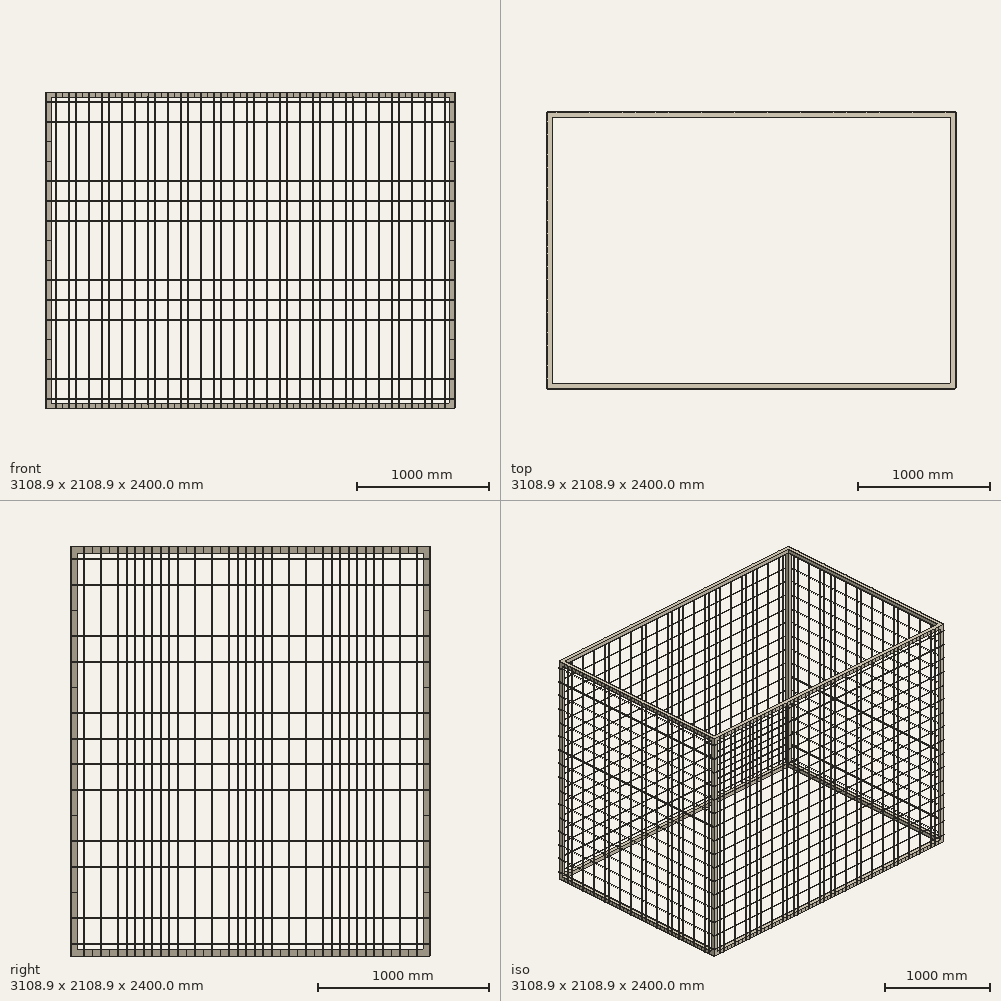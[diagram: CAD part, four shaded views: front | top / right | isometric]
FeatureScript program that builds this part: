
annotation { "Feature Type Name" : "Feature", "Feature Type Description" : "" }
export const myFeature = defineFeature(function(context is Context, id is Id, definition is map)
    precondition{}
    {
        {
            var Q0;
            Q0=qCreatedBy(makeId("Top.planeOp"),FACE);
            var sketch = newSketch(context, id + "F0", { "sketchPlane" : qUnion([Q0])});
            skLineSegment(sketch, "E0", {"start": v(-1510, 0) * mm, "end": v(-1550, 0) * mm});
            skLineSegment(sketch, "E1", {"start": v(-1550, 0) * mm, "end": v(-1550, -1050) * mm});
            skLineSegment(sketch, "E2", {"start": v(-1550, -1050) * mm, "end": v(0, -1050) * mm});
            skLineSegment(sketch, "E3", {"start": v(0, -1050) * mm, "end": v(0, -1010) * mm});
            skLineSegment(sketch, "E4", {"start": v(0, -1010) * mm, "end": v(-1510, -1010) * mm});
            skLineSegment(sketch, "E5", {"start": v(-1510, 0) * mm, "end": v(-1510, -1010) * mm});
            skLineSegment(sketch, "E6", {"start": v(0, 0) * mm, "end": v(0, 100.18) * mm, "construction": true});
            skLineSegment(sketch, "E7", {"start": v(0, 0) * mm, "end": v(-123.05, 0) * mm, "construction": true});
            skSolve(sketch);
        }
        {
            var Q0;
            Q0 = qSketchRegion(id + "F0", true);
            extrude(context, id + "F1", {"entities" : qUnion([Q0]), "depth" : 40 * mm});
        }
        {
            var Q0;
            Q0=qCreatedBy(makeId("Top.planeOp"),FACE);
            var sketch = newSketch(context, id + "F2", { "sketchPlane" : qUnion([Q0])});
            skLineSegment(sketch, "E8.bottom", {"start": v(-1550, -1010) * mm, "end": v(-1510, -1010) * mm});
            skLineSegment(sketch, "E8.top", {"start": v(-1550, -1050) * mm, "end": v(-1510, -1050) * mm});
            skLineSegment(sketch, "E8.left", {"start": v(-1550, -1010) * mm, "end": v(-1550, -1050) * mm});
            skLineSegment(sketch, "E8.right", {"start": v(-1510, -1010) * mm, "end": v(-1510, -1050) * mm});
            skSolve(sketch);
        }
        {
            var Q0;
            Q0 = qSketchRegion(id + "F2", true);
            extrude(context, id + "F3", {"entities" : qUnion([Q0]), "operationType" : NewBodyOperationType.ADD, "depth" : 1200 * mm});
        }
        {
            var Q0;
            Q0=qCreatedBy(makeId("Top.planeOp"),FACE);
            var sketch = newSketch(context, id + "F4", { "sketchPlane" : qUnion([Q0])});
            skCircle(sketch, "E9", {"center": v(-1552.2, -25) * mm, "radius": 2.25 * mm});
            skLineSegment(sketch, "E10", {"start": v(-121.65, 0) * mm, "end": v(-1550, 0) * mm, "construction": true});
            skLineSegment(sketch, "E11", {"start": v(0, -80.6) * mm, "end": v(0, -1050) * mm, "construction": true});
            skCircle(sketch, "E12", {"center": v(-25, -1052.2) * mm, "radius": 2.25 * mm});
            skCircle(sketch, "E13.1.0.0", {"center": v(-75, -1052.2) * mm, "radius": 2.25 * mm});
            skCircle(sketch, "E13.2.0.0", {"center": v(-125, -1052.2) * mm, "radius": 2.25 * mm});
            skCircle(sketch, "E13.3.0.0", {"center": v(-175, -1052.2) * mm, "radius": 2.25 * mm});
            skCircle(sketch, "E13.4.0.0", {"center": v(-225, -1052.2) * mm, "radius": 2.25 * mm});
            skCircle(sketch, "E13.5.0.0", {"center": v(-275, -1052.2) * mm, "radius": 2.25 * mm});
            skCircle(sketch, "E13.6.0.0", {"center": v(-325, -1052.2) * mm, "radius": 2.25 * mm});
            skCircle(sketch, "E13.7.0.0", {"center": v(-375, -1052.2) * mm, "radius": 2.25 * mm});
            skCircle(sketch, "E13.8.0.0", {"center": v(-425, -1052.2) * mm, "radius": 2.25 * mm});
            skCircle(sketch, "E13.9.0.0", {"center": v(-475, -1052.2) * mm, "radius": 2.25 * mm});
            skCircle(sketch, "E13.10.0.0", {"center": v(-525, -1052.2) * mm, "radius": 2.25 * mm});
            skCircle(sketch, "E13.11.0.0", {"center": v(-575, -1052.2) * mm, "radius": 2.25 * mm});
            skCircle(sketch, "E13.12.0.0", {"center": v(-625, -1052.2) * mm, "radius": 2.25 * mm});
            skCircle(sketch, "E13.13.0.0", {"center": v(-675, -1052.2) * mm, "radius": 2.25 * mm});
            skCircle(sketch, "E13.14.0.0", {"center": v(-725, -1052.2) * mm, "radius": 2.25 * mm});
            skCircle(sketch, "E13.15.0.0", {"center": v(-775, -1052.2) * mm, "radius": 2.25 * mm});
            skCircle(sketch, "E13.16.0.0", {"center": v(-825, -1052.2) * mm, "radius": 2.25 * mm});
            skCircle(sketch, "E13.17.0.0", {"center": v(-875, -1052.2) * mm, "radius": 2.25 * mm});
            skCircle(sketch, "E13.18.0.0", {"center": v(-925, -1052.2) * mm, "radius": 2.25 * mm});
            skCircle(sketch, "E13.19.0.0", {"center": v(-975, -1052.2) * mm, "radius": 2.25 * mm});
            skCircle(sketch, "E13.20.0.0", {"center": v(-1025, -1052.2) * mm, "radius": 2.25 * mm});
            skCircle(sketch, "E13.21.0.0", {"center": v(-1075, -1052.2) * mm, "radius": 2.25 * mm});
            skCircle(sketch, "E13.22.0.0", {"center": v(-1125, -1052.2) * mm, "radius": 2.25 * mm});
            skCircle(sketch, "E13.23.0.0", {"center": v(-1175, -1052.2) * mm, "radius": 2.25 * mm});
            skCircle(sketch, "E13.24.0.0", {"center": v(-1225, -1052.2) * mm, "radius": 2.25 * mm});
            skCircle(sketch, "E13.25.0.0", {"center": v(-1275, -1052.2) * mm, "radius": 2.25 * mm});
            skCircle(sketch, "E13.26.0.0", {"center": v(-1325, -1052.2) * mm, "radius": 2.25 * mm});
            skCircle(sketch, "E13.27.0.0", {"center": v(-1375, -1052.2) * mm, "radius": 2.25 * mm});
            skCircle(sketch, "E13.28.0.0", {"center": v(-1425, -1052.2) * mm, "radius": 2.25 * mm});
            skCircle(sketch, "E13.29.0.0", {"center": v(-1475, -1052.2) * mm, "radius": 2.25 * mm});
            skLineSegment(sketch, "E13.direction1", {"start": v(-25, -1052.2) * mm, "end": v(-75, -1052.2) * mm, "construction": true});
            skCircle(sketch, "E14.0.1.0", {"center": v(-1552.2, -75) * mm, "radius": 2.25 * mm});
            skCircle(sketch, "E14.0.2.0", {"center": v(-1552.2, -125) * mm, "radius": 2.25 * mm});
            skCircle(sketch, "E14.0.3.0", {"center": v(-1552.2, -175) * mm, "radius": 2.25 * mm});
            skCircle(sketch, "E14.0.4.0", {"center": v(-1552.2, -225) * mm, "radius": 2.25 * mm});
            skCircle(sketch, "E14.0.5.0", {"center": v(-1552.2, -275) * mm, "radius": 2.25 * mm});
            skCircle(sketch, "E14.0.6.0", {"center": v(-1552.2, -325) * mm, "radius": 2.25 * mm});
            skCircle(sketch, "E14.0.7.0", {"center": v(-1552.2, -375) * mm, "radius": 2.25 * mm});
            skCircle(sketch, "E14.0.8.0", {"center": v(-1552.2, -425) * mm, "radius": 2.25 * mm});
            skCircle(sketch, "E14.0.9.0", {"center": v(-1552.2, -475) * mm, "radius": 2.25 * mm});
            skCircle(sketch, "E14.0.10.0", {"center": v(-1552.2, -525) * mm, "radius": 2.25 * mm});
            skCircle(sketch, "E14.0.11.0", {"center": v(-1552.2, -575) * mm, "radius": 2.25 * mm});
            skCircle(sketch, "E14.0.12.0", {"center": v(-1552.2, -625) * mm, "radius": 2.25 * mm});
            skCircle(sketch, "E14.0.13.0", {"center": v(-1552.2, -675) * mm, "radius": 2.25 * mm});
            skCircle(sketch, "E14.0.14.0", {"center": v(-1552.2, -725) * mm, "radius": 2.25 * mm});
            skCircle(sketch, "E14.0.15.0", {"center": v(-1552.2, -775) * mm, "radius": 2.25 * mm});
            skCircle(sketch, "E14.0.16.0", {"center": v(-1552.2, -825) * mm, "radius": 2.25 * mm});
            skCircle(sketch, "E14.0.17.0", {"center": v(-1552.2, -875) * mm, "radius": 2.25 * mm});
            skCircle(sketch, "E14.0.18.0", {"center": v(-1552.2, -925) * mm, "radius": 2.25 * mm});
            skCircle(sketch, "E14.0.19.0", {"center": v(-1552.2, -975) * mm, "radius": 2.25 * mm});
            skLineSegment(sketch, "E14.direction1", {"start": v(-1552.2, -25) * mm, "end": v(-1527.2, -25) * mm, "construction": true});
            skLineSegment(sketch, "E14.direction2", {"start": v(-1552.2, -25) * mm, "end": v(-1552.2, -75) * mm, "construction": true});
            skSolve(sketch);
        }
        {
            var Q0;
            Q0 = qSketchRegion(id + "F4", true);
            var Q1;
            Q1=makeQuery(id+"F3.opExtrude","CAP_FACE",FACE,{"disambiguationData":[OSD([sQuery(id+"F2.wireOp",EDGE,"E8.bottom"),sQuery(id+"F2.wireOp",EDGE,"E8.top"),sQuery(id+"F2.wireOp",EDGE,"E8.left"),sQuery(id+"F2.wireOp",EDGE,"E8.right")])],"isStart":false});
            extrude(context, id + "F5", {"entities" : qUnion([Q0]), "operationType" : NewBodyOperationType.ADD, "endBound" : BoundingType.UP_TO_SURFACE, "endBoundEntityFace" : qUnion([Q1]), "depth" : 25 * mm});
        }
        {
            var Q0;
            Q0=qCreatedBy(makeId("Front.planeOp"),FACE);
            var sketch = newSketch(context, id + "F6", { "sketchPlane" : qUnion([Q0])});
            skLineSegment(sketch, "E15.0", {"start": v(-1554.45, 1200) * mm, "end": v(-1549.95, 1200) * mm, "construction": true});
            skLineSegment(sketch, "E16", {"start": v(-1554.45, 1200) * mm, "end": v(-1554.45, 1217.11) * mm, "construction": true});
            skLineSegment(sketch, "E17", {"start": v(-1549.95, 1200) * mm, "end": v(-1549.95, 1218.1) * mm, "construction": true});
            skCircle(sketch, "E18", {"center": v(-1552.2, 1125) * mm, "radius": 2.25 * mm});
            skCircle(sketch, "E19.0.1.0", {"center": v(-1552.2, 975) * mm, "radius": 2.25 * mm});
            skCircle(sketch, "E19.0.2.0", {"center": v(-1552.2, 825) * mm, "radius": 2.25 * mm});
            skCircle(sketch, "E19.0.3.0", {"center": v(-1552.2, 675) * mm, "radius": 2.25 * mm});
            skCircle(sketch, "E19.0.4.0", {"center": v(-1552.2, 525) * mm, "radius": 2.25 * mm});
            skCircle(sketch, "E19.0.5.0", {"center": v(-1552.2, 375) * mm, "radius": 2.25 * mm});
            skCircle(sketch, "E19.0.6.0", {"center": v(-1552.2, 225) * mm, "radius": 2.25 * mm});
            skCircle(sketch, "E19.0.7.0", {"center": v(-1552.2, 75) * mm, "radius": 2.25 * mm});
            skLineSegment(sketch, "E19.direction1", {"start": v(-1552.2, 1125) * mm, "end": v(-1527.2, 1125) * mm, "construction": true});
            skLineSegment(sketch, "E19.direction2", {"start": v(-1552.2, 1125) * mm, "end": v(-1552.2, 975) * mm, "construction": true});
            skSolve(sketch);
        }
        {
            var Q0;
            Q0 = qSketchRegion(id + "F6", true);
            var Q1;
            {var subQ0=sQuery(id+"F4.wireOp",EDGE,"E13.29.0.0");var subQ1=sQuery(id+"F0.wireOp",EDGE,"E1");var subQ2=sQuery(id+"F0.wireOp",EDGE,"E5");var subQ3=sQuery(id+"F0.wireOp",EDGE,"E4");var subQ4=sQuery(id+"F0.wireOp",EDGE,"E3");var subQ5=sQuery(id+"F0.wireOp",EDGE,"E2");var subQ6=sQuery(id+"F0.wireOp",EDGE,"E0");var subQ7=sQuery(id+"F2.wireOp",EDGE,"E8.left");var subQ8=sQuery(id+"F2.wireOp",EDGE,"E8.right");var subQ9=sQuery(id+"F2.wireOp",EDGE,"E8.top");Q1=makeQuery(id+"F5.boolean.opBoolean","SPLIT",FACE,{"disambiguationData":[TD([makeQuery(id+"F1.opExtrude","CAP_FACE",FACE,{"disambiguationData":[OSD([subQ6,subQ1,subQ5,subQ4,subQ3,subQ2])],"isStart":true}),makeQuery(id+"F1.opExtrude","CAP_FACE",FACE,{"disambiguationData":[OSD([subQ6,subQ1,subQ5,subQ4,subQ3,subQ2])],"isStart":false}),makeQuery(id+"F1.opExtrude","SWEPT_FACE",FACE,{"disambiguationData":[OSD([subQ1])]}),makeQuery(id+"F3.opExtrude","CAP_FACE",FACE,{"disambiguationData":[OSD([sQuery(id+"F2.wireOp",EDGE,"E8.bottom"),subQ9,subQ7,subQ8])],"isStart":false}),makeQuery(id+"F3.opExtrude","SWEPT_FACE",FACE,{"disambiguationData":[OSD([subQ7])]}),makeQuery(id+"F3.opExtrude","SWEPT_FACE",FACE,{"disambiguationData":[OSD([subQ8])]}),makeQuery(id+"F5.opExtrude","CAP_FACE",FACE,{"disambiguationData":[OSD([sQuery(id+"F4.wireOp",EDGE,"E9")])],"isStart":true}),makeQuery(id+"F5.opExtrude","CAP_FACE",FACE,{"disambiguationData":[OSD([sQuery(id+"F4.wireOp",EDGE,"E12")])],"isStart":true}),makeQuery(id+"F5.opExtrude","CAP_FACE",FACE,{"disambiguationData":[OSD([sQuery(id+"F4.wireOp",EDGE,"E13.1.0.0")])],"isStart":true}),makeQuery(id+"F5.opExtrude","CAP_FACE",FACE,{"disambiguationData":[OSD([sQuery(id+"F4.wireOp",EDGE,"E13.2.0.0")])],"isStart":true}),makeQuery(id+"F5.opExtrude","CAP_FACE",FACE,{"disambiguationData":[OSD([sQuery(id+"F4.wireOp",EDGE,"E13.3.0.0")])],"isStart":true}),makeQuery(id+"F5.opExtrude","CAP_FACE",FACE,{"disambiguationData":[OSD([sQuery(id+"F4.wireOp",EDGE,"E13.4.0.0")])],"isStart":true}),makeQuery(id+"F5.opExtrude","CAP_FACE",FACE,{"disambiguationData":[OSD([sQuery(id+"F4.wireOp",EDGE,"E13.5.0.0")])],"isStart":true}),makeQuery(id+"F5.opExtrude","CAP_FACE",FACE,{"disambiguationData":[OSD([sQuery(id+"F4.wireOp",EDGE,"E13.6.0.0")])],"isStart":true}),makeQuery(id+"F5.opExtrude","CAP_FACE",FACE,{"disambiguationData":[OSD([sQuery(id+"F4.wireOp",EDGE,"E13.7.0.0")])],"isStart":true}),makeQuery(id+"F5.opExtrude","CAP_FACE",FACE,{"disambiguationData":[OSD([sQuery(id+"F4.wireOp",EDGE,"E13.8.0.0")])],"isStart":true}),makeQuery(id+"F5.opExtrude","CAP_FACE",FACE,{"disambiguationData":[OSD([sQuery(id+"F4.wireOp",EDGE,"E13.9.0.0")])],"isStart":true}),makeQuery(id+"F5.opExtrude","CAP_FACE",FACE,{"disambiguationData":[OSD([sQuery(id+"F4.wireOp",EDGE,"E13.10.0.0")])],"isStart":true}),makeQuery(id+"F5.opExtrude","CAP_FACE",FACE,{"disambiguationData":[OSD([sQuery(id+"F4.wireOp",EDGE,"E13.11.0.0")])],"isStart":true}),makeQuery(id+"F5.opExtrude","CAP_FACE",FACE,{"disambiguationData":[OSD([sQuery(id+"F4.wireOp",EDGE,"E13.12.0.0")])],"isStart":true}),makeQuery(id+"F5.opExtrude","CAP_FACE",FACE,{"disambiguationData":[OSD([sQuery(id+"F4.wireOp",EDGE,"E13.13.0.0")])],"isStart":true}),makeQuery(id+"F5.opExtrude","CAP_FACE",FACE,{"disambiguationData":[OSD([sQuery(id+"F4.wireOp",EDGE,"E13.14.0.0")])],"isStart":true}),makeQuery(id+"F5.opExtrude","CAP_FACE",FACE,{"disambiguationData":[OSD([sQuery(id+"F4.wireOp",EDGE,"E13.15.0.0")])],"isStart":true}),makeQuery(id+"F5.opExtrude","CAP_FACE",FACE,{"disambiguationData":[OSD([sQuery(id+"F4.wireOp",EDGE,"E13.16.0.0")])],"isStart":true}),makeQuery(id+"F5.opExtrude","CAP_FACE",FACE,{"disambiguationData":[OSD([sQuery(id+"F4.wireOp",EDGE,"E13.17.0.0")])],"isStart":true}),makeQuery(id+"F5.opExtrude","CAP_FACE",FACE,{"disambiguationData":[OSD([sQuery(id+"F4.wireOp",EDGE,"E13.18.0.0")])],"isStart":true}),makeQuery(id+"F5.opExtrude","CAP_FACE",FACE,{"disambiguationData":[OSD([sQuery(id+"F4.wireOp",EDGE,"E13.19.0.0")])],"isStart":true}),makeQuery(id+"F5.opExtrude","CAP_FACE",FACE,{"disambiguationData":[OSD([sQuery(id+"F4.wireOp",EDGE,"E13.20.0.0")])],"isStart":true}),makeQuery(id+"F5.opExtrude","CAP_FACE",FACE,{"disambiguationData":[OSD([sQuery(id+"F4.wireOp",EDGE,"E13.21.0.0")])],"isStart":true}),makeQuery(id+"F5.opExtrude","CAP_FACE",FACE,{"disambiguationData":[OSD([sQuery(id+"F4.wireOp",EDGE,"E13.22.0.0")])],"isStart":true}),makeQuery(id+"F5.opExtrude","CAP_FACE",FACE,{"disambiguationData":[OSD([sQuery(id+"F4.wireOp",EDGE,"E13.23.0.0")])],"isStart":true}),makeQuery(id+"F5.opExtrude","CAP_FACE",FACE,{"disambiguationData":[OSD([sQuery(id+"F4.wireOp",EDGE,"E13.24.0.0")])],"isStart":true}),makeQuery(id+"F5.opExtrude","CAP_FACE",FACE,{"disambiguationData":[OSD([sQuery(id+"F4.wireOp",EDGE,"E13.25.0.0")])],"isStart":true}),makeQuery(id+"F5.opExtrude","CAP_FACE",FACE,{"disambiguationData":[OSD([sQuery(id+"F4.wireOp",EDGE,"E13.26.0.0")])],"isStart":true}),makeQuery(id+"F5.opExtrude","CAP_FACE",FACE,{"disambiguationData":[OSD([sQuery(id+"F4.wireOp",EDGE,"E13.27.0.0")])],"isStart":true}),makeQuery(id+"F5.opExtrude","CAP_FACE",FACE,{"disambiguationData":[OSD([sQuery(id+"F4.wireOp",EDGE,"E13.28.0.0")])],"isStart":true}),makeQuery(id+"F5.opExtrude","SWEPT_FACE",FACE,{"disambiguationData":[OSD([subQ0])]}),makeQuery(id+"F5.opExtrude","CAP_FACE",FACE,{"disambiguationData":[OSD([subQ0])],"isStart":true}),makeQuery(id+"F5.opExtrude","CAP_FACE",FACE,{"disambiguationData":[OSD([sQuery(id+"F4.wireOp",EDGE,"E14.0.1.0")])],"isStart":true}),makeQuery(id+"F5.opExtrude","CAP_FACE",FACE,{"disambiguationData":[OSD([sQuery(id+"F4.wireOp",EDGE,"E14.0.2.0")])],"isStart":true}),makeQuery(id+"F5.opExtrude","CAP_FACE",FACE,{"disambiguationData":[OSD([sQuery(id+"F4.wireOp",EDGE,"E14.0.3.0")])],"isStart":true}),makeQuery(id+"F5.opExtrude","CAP_FACE",FACE,{"disambiguationData":[OSD([sQuery(id+"F4.wireOp",EDGE,"E14.0.4.0")])],"isStart":true}),makeQuery(id+"F5.opExtrude","CAP_FACE",FACE,{"disambiguationData":[OSD([sQuery(id+"F4.wireOp",EDGE,"E14.0.5.0")])],"isStart":true}),makeQuery(id+"F5.opExtrude","CAP_FACE",FACE,{"disambiguationData":[OSD([sQuery(id+"F4.wireOp",EDGE,"E14.0.6.0")])],"isStart":true}),makeQuery(id+"F5.opExtrude","CAP_FACE",FACE,{"disambiguationData":[OSD([sQuery(id+"F4.wireOp",EDGE,"E14.0.7.0")])],"isStart":true}),makeQuery(id+"F5.opExtrude","CAP_FACE",FACE,{"disambiguationData":[OSD([sQuery(id+"F4.wireOp",EDGE,"E14.0.8.0")])],"isStart":true}),makeQuery(id+"F5.opExtrude","CAP_FACE",FACE,{"disambiguationData":[OSD([sQuery(id+"F4.wireOp",EDGE,"E14.0.9.0")])],"isStart":true}),makeQuery(id+"F5.opExtrude","CAP_FACE",FACE,{"disambiguationData":[OSD([sQuery(id+"F4.wireOp",EDGE,"E14.0.10.0")])],"isStart":true}),makeQuery(id+"F5.opExtrude","CAP_FACE",FACE,{"disambiguationData":[OSD([sQuery(id+"F4.wireOp",EDGE,"E14.0.11.0")])],"isStart":true}),makeQuery(id+"F5.opExtrude","CAP_FACE",FACE,{"disambiguationData":[OSD([sQuery(id+"F4.wireOp",EDGE,"E14.0.12.0")])],"isStart":true}),makeQuery(id+"F5.opExtrude","CAP_FACE",FACE,{"disambiguationData":[OSD([sQuery(id+"F4.wireOp",EDGE,"E14.0.13.0")])],"isStart":true}),makeQuery(id+"F5.opExtrude","CAP_FACE",FACE,{"disambiguationData":[OSD([sQuery(id+"F4.wireOp",EDGE,"E14.0.14.0")])],"isStart":true}),makeQuery(id+"F5.opExtrude","CAP_FACE",FACE,{"disambiguationData":[OSD([sQuery(id+"F4.wireOp",EDGE,"E14.0.15.0")])],"isStart":true}),makeQuery(id+"F5.opExtrude","CAP_FACE",FACE,{"disambiguationData":[OSD([sQuery(id+"F4.wireOp",EDGE,"E14.0.16.0")])],"isStart":true}),makeQuery(id+"F5.opExtrude","CAP_FACE",FACE,{"disambiguationData":[OSD([sQuery(id+"F4.wireOp",EDGE,"E14.0.17.0")])],"isStart":true}),makeQuery(id+"F5.opExtrude","CAP_FACE",FACE,{"disambiguationData":[OSD([sQuery(id+"F4.wireOp",EDGE,"E14.0.18.0")])],"isStart":true}),makeQuery(id+"F5.opExtrude","CAP_FACE",FACE,{"disambiguationData":[OSD([sQuery(id+"F4.wireOp",EDGE,"E14.0.19.0")])],"isStart":true})])],"derivedFrom":makeQuery(id+"F3.boolean.opBoolean","MERGE",FACE,{"derivedFrom":[makeQuery(id+"F1.opExtrude","SWEPT_FACE",FACE,{"disambiguationData":[OSD([subQ5])]}),makeQuery(id+"F3.opExtrude","SWEPT_FACE",FACE,{"disambiguationData":[OSD([subQ9])]})]})});}
            extrude(context, id + "F7", {"entities" : qUnion([Q0]), "operationType" : NewBodyOperationType.ADD, "endBound" : BoundingType.UP_TO_SURFACE, "endBoundEntityFace" : qUnion([Q1]), "depth" : 25 * mm});
        }
        {
            var Q0;
            Q0=qCreatedBy(makeId("Right.planeOp"),FACE);
            var sketch = newSketch(context, id + "F8", { "sketchPlane" : qUnion([Q0])});
            skCircle(sketch, "E20", {"center": v(-1052.2, 1125) * mm, "radius": 2.25 * mm});
            skLineSegment(sketch, "E21.0", {"start": v(-1054.45, 1200) * mm, "end": v(-1049.95, 1200) * mm, "construction": true});
            skLineSegment(sketch, "E22", {"start": v(-1049.95, 1200) * mm, "end": v(-1049.95, 1213.47) * mm, "construction": true});
            skLineSegment(sketch, "E23", {"start": v(-1054.45, 1200) * mm, "end": v(-1054.45, 1213.32) * mm, "construction": true});
            skCircle(sketch, "E24.0.1.0", {"center": v(-1052.2, 975) * mm, "radius": 2.25 * mm});
            skCircle(sketch, "E24.0.2.0", {"center": v(-1052.2, 825) * mm, "radius": 2.25 * mm});
            skCircle(sketch, "E24.0.3.0", {"center": v(-1052.2, 675) * mm, "radius": 2.25 * mm});
            skCircle(sketch, "E24.0.4.0", {"center": v(-1052.2, 525) * mm, "radius": 2.25 * mm});
            skCircle(sketch, "E24.0.5.0", {"center": v(-1052.2, 375) * mm, "radius": 2.25 * mm});
            skCircle(sketch, "E24.0.6.0", {"center": v(-1052.2, 225) * mm, "radius": 2.25 * mm});
            skCircle(sketch, "E24.0.7.0", {"center": v(-1052.2, 75) * mm, "radius": 2.25 * mm});
            skLineSegment(sketch, "E24.direction1", {"start": v(-1052.2, 1125) * mm, "end": v(-1027.2, 1125) * mm, "construction": true});
            skLineSegment(sketch, "E24.direction2", {"start": v(-1052.2, 1125) * mm, "end": v(-1052.2, 975) * mm, "construction": true});
            skSolve(sketch);
        }
        {
            var Q0;
            Q0 = qSketchRegion(id + "F8", true);
            var Q1;
            {var subQ0=makeQuery(id+"F5.opExtrude","CAP_FACE",FACE,{"disambiguationData":[OSD([sQuery(id+"F4.wireOp",EDGE,"E14.0.10.0")])],"isStart":true});var subQ1=makeQuery(id+"F5.opExtrude","CAP_FACE",FACE,{"disambiguationData":[OSD([sQuery(id+"F4.wireOp",EDGE,"E13.3.0.0")])],"isStart":true});var subQ2=makeQuery(id+"F5.opExtrude","CAP_FACE",FACE,{"disambiguationData":[OSD([sQuery(id+"F4.wireOp",EDGE,"E14.0.8.0")])],"isStart":true});var subQ3=makeQuery(id+"F5.opExtrude","CAP_FACE",FACE,{"disambiguationData":[OSD([sQuery(id+"F4.wireOp",EDGE,"E14.0.9.0")])],"isStart":true});var subQ4=makeQuery(id+"F5.opExtrude","CAP_FACE",FACE,{"disambiguationData":[OSD([sQuery(id+"F4.wireOp",EDGE,"E14.0.6.0")])],"isStart":true});var subQ5=makeQuery(id+"F5.opExtrude","CAP_FACE",FACE,{"disambiguationData":[OSD([sQuery(id+"F4.wireOp",EDGE,"E14.0.7.0")])],"isStart":true});var subQ6=makeQuery(id+"F5.opExtrude","CAP_FACE",FACE,{"disambiguationData":[OSD([sQuery(id+"F4.wireOp",EDGE,"E14.0.4.0")])],"isStart":true});var subQ7=makeQuery(id+"F5.opExtrude","CAP_FACE",FACE,{"disambiguationData":[OSD([sQuery(id+"F4.wireOp",EDGE,"E13.12.0.0")])],"isStart":true});var subQ8=makeQuery(id+"F5.opExtrude","CAP_FACE",FACE,{"disambiguationData":[OSD([sQuery(id+"F4.wireOp",EDGE,"E14.0.5.0")])],"isStart":true});var subQ9=makeQuery(id+"F5.opExtrude","CAP_FACE",FACE,{"disambiguationData":[OSD([sQuery(id+"F4.wireOp",EDGE,"E14.0.2.0")])],"isStart":true});var subQ10=makeQuery(id+"F5.opExtrude","CAP_FACE",FACE,{"disambiguationData":[OSD([sQuery(id+"F4.wireOp",EDGE,"E13.10.0.0")])],"isStart":true});var subQ11=makeQuery(id+"F5.opExtrude","CAP_FACE",FACE,{"disambiguationData":[OSD([sQuery(id+"F4.wireOp",EDGE,"E13.27.0.0")])],"isStart":true});var subQ12=makeQuery(id+"F5.opExtrude","CAP_FACE",FACE,{"disambiguationData":[OSD([sQuery(id+"F4.wireOp",EDGE,"E13.28.0.0")])],"isStart":true});var subQ13=makeQuery(id+"F5.opExtrude","CAP_FACE",FACE,{"disambiguationData":[OSD([sQuery(id+"F4.wireOp",EDGE,"E13.25.0.0")])],"isStart":true});var subQ14=makeQuery(id+"F5.opExtrude","CAP_FACE",FACE,{"disambiguationData":[OSD([sQuery(id+"F4.wireOp",EDGE,"E13.24.0.0")])],"isStart":true});var subQ15=makeQuery(id+"F5.opExtrude","CAP_FACE",FACE,{"disambiguationData":[OSD([sQuery(id+"F4.wireOp",EDGE,"E14.0.16.0")])],"isStart":true});var subQ16=makeQuery(id+"F5.opExtrude","CAP_FACE",FACE,{"disambiguationData":[OSD([sQuery(id+"F4.wireOp",EDGE,"E13.26.0.0")])],"isStart":true});var subQ17=makeQuery(id+"F5.opExtrude","CAP_FACE",FACE,{"disambiguationData":[OSD([sQuery(id+"F4.wireOp",EDGE,"E14.0.18.0")])],"isStart":true});var subQ18=makeQuery(id+"F5.opExtrude","CAP_FACE",FACE,{"disambiguationData":[OSD([sQuery(id+"F4.wireOp",EDGE,"E13.23.0.0")])],"isStart":true});var subQ19=makeQuery(id+"F5.opExtrude","CAP_FACE",FACE,{"disambiguationData":[OSD([sQuery(id+"F4.wireOp",EDGE,"E13.21.0.0")])],"isStart":true});var subQ20=makeQuery(id+"F5.opExtrude","CAP_FACE",FACE,{"disambiguationData":[OSD([sQuery(id+"F4.wireOp",EDGE,"E13.22.0.0")])],"isStart":true});var subQ21=makeQuery(id+"F5.opExtrude","CAP_FACE",FACE,{"disambiguationData":[OSD([sQuery(id+"F4.wireOp",EDGE,"E13.19.0.0")])],"isStart":true});var subQ22=makeQuery(id+"F5.opExtrude","CAP_FACE",FACE,{"disambiguationData":[OSD([sQuery(id+"F4.wireOp",EDGE,"E13.20.0.0")])],"isStart":true});var subQ23=makeQuery(id+"F5.opExtrude","CAP_FACE",FACE,{"disambiguationData":[OSD([sQuery(id+"F4.wireOp",EDGE,"E13.17.0.0")])],"isStart":true});var subQ24=makeQuery(id+"F5.opExtrude","CAP_FACE",FACE,{"disambiguationData":[OSD([sQuery(id+"F4.wireOp",EDGE,"E12")])],"isStart":true});var subQ25=makeQuery(id+"F5.opExtrude","CAP_FACE",FACE,{"disambiguationData":[OSD([sQuery(id+"F4.wireOp",EDGE,"E13.2.0.0")])],"isStart":true});var subQ26=makeQuery(id+"F5.opExtrude","CAP_FACE",FACE,{"disambiguationData":[OSD([sQuery(id+"F4.wireOp",EDGE,"E9")])],"isStart":true});var subQ27=makeQuery(id+"F5.opExtrude","CAP_FACE",FACE,{"disambiguationData":[OSD([sQuery(id+"F4.wireOp",EDGE,"E13.16.0.0")])],"isStart":true});var subQ28=sQuery(id+"F2.wireOp",EDGE,"E8.top");var subQ29=makeQuery(id+"F3.opExtrude","SWEPT_FACE",FACE,{"disambiguationData":[OSD([subQ28])]});var subQ30=makeQuery(id+"F5.opExtrude","CAP_FACE",FACE,{"disambiguationData":[OSD([sQuery(id+"F4.wireOp",EDGE,"E13.18.0.0")])],"isStart":true});var subQ31=sQuery(id+"F0.wireOp",EDGE,"E5");var subQ32=sQuery(id+"F0.wireOp",EDGE,"E4");var subQ33=sQuery(id+"F0.wireOp",EDGE,"E3");var subQ34=sQuery(id+"F0.wireOp",EDGE,"E2");var subQ35=sQuery(id+"F0.wireOp",EDGE,"E1");var subQ36=sQuery(id+"F0.wireOp",EDGE,"E0");var subQ37=makeQuery(id+"F1.opExtrude","CAP_FACE",FACE,{"disambiguationData":[OSD([subQ36,subQ35,subQ34,subQ33,subQ32,subQ31])],"isStart":true});var subQ38=makeQuery(id+"F5.opExtrude","CAP_FACE",FACE,{"disambiguationData":[OSD([sQuery(id+"F4.wireOp",EDGE,"E13.15.0.0")])],"isStart":true});var subQ39=makeQuery(id+"F5.opExtrude","CAP_FACE",FACE,{"disambiguationData":[OSD([sQuery(id+"F4.wireOp",EDGE,"E13.14.0.0")])],"isStart":true});var subQ40=makeQuery(id+"F1.opExtrude","SWEPT_FACE",FACE,{"disambiguationData":[OSD([subQ34])]});var subQ41=makeQuery(id+"F5.opExtrude","CAP_FACE",FACE,{"disambiguationData":[OSD([sQuery(id+"F4.wireOp",EDGE,"E14.0.3.0")])],"isStart":true});var subQ42=makeQuery(id+"F5.opExtrude","CAP_FACE",FACE,{"disambiguationData":[OSD([sQuery(id+"F4.wireOp",EDGE,"E13.29.0.0")])],"isStart":true});var subQ43=makeQuery(id+"F5.opExtrude","CAP_FACE",FACE,{"disambiguationData":[OSD([sQuery(id+"F4.wireOp",EDGE,"E13.8.0.0")])],"isStart":true});var subQ44=makeQuery(id+"F5.opExtrude","CAP_FACE",FACE,{"disambiguationData":[OSD([sQuery(id+"F4.wireOp",EDGE,"E13.13.0.0")])],"isStart":true});var subQ45=makeQuery(id+"F5.opExtrude","CAP_FACE",FACE,{"disambiguationData":[OSD([sQuery(id+"F4.wireOp",EDGE,"E13.1.0.0")])],"isStart":true});var subQ46=makeQuery(id+"F5.opExtrude","CAP_FACE",FACE,{"disambiguationData":[OSD([sQuery(id+"F4.wireOp",EDGE,"E13.4.0.0")])],"isStart":true});var subQ47=makeQuery(id+"F5.opExtrude","CAP_FACE",FACE,{"disambiguationData":[OSD([sQuery(id+"F4.wireOp",EDGE,"E14.0.11.0")])],"isStart":true});var subQ48=makeQuery(id+"F1.opExtrude","CAP_FACE",FACE,{"disambiguationData":[OSD([subQ36,subQ35,subQ34,subQ33,subQ32,subQ31])],"isStart":false});var subQ49=makeQuery(id+"F5.opExtrude","CAP_FACE",FACE,{"disambiguationData":[OSD([sQuery(id+"F4.wireOp",EDGE,"E13.5.0.0")])],"isStart":true});var subQ50=makeQuery(id+"F5.opExtrude","CAP_FACE",FACE,{"disambiguationData":[OSD([sQuery(id+"F4.wireOp",EDGE,"E14.0.12.0")])],"isStart":true});var subQ51=makeQuery(id+"F5.opExtrude","CAP_FACE",FACE,{"disambiguationData":[OSD([sQuery(id+"F4.wireOp",EDGE,"E13.6.0.0")])],"isStart":true});var subQ52=makeQuery(id+"F5.opExtrude","CAP_FACE",FACE,{"disambiguationData":[OSD([sQuery(id+"F4.wireOp",EDGE,"E14.0.13.0")])],"isStart":true});var subQ53=makeQuery(id+"F5.opExtrude","CAP_FACE",FACE,{"disambiguationData":[OSD([sQuery(id+"F4.wireOp",EDGE,"E13.7.0.0")])],"isStart":true});var subQ54=sQuery(id+"F2.wireOp",EDGE,"E8.bottom");var subQ55=makeQuery(id+"F3.opExtrude","SWEPT_FACE",FACE,{"disambiguationData":[OSD([subQ54])]});var subQ56=makeQuery(id+"F5.opExtrude","CAP_FACE",FACE,{"disambiguationData":[OSD([sQuery(id+"F4.wireOp",EDGE,"E14.0.1.0")])],"isStart":true});var subQ57=makeQuery(id+"F5.opExtrude","CAP_FACE",FACE,{"disambiguationData":[OSD([sQuery(id+"F4.wireOp",EDGE,"E13.11.0.0")])],"isStart":true});var subQ58=makeQuery(id+"F5.opExtrude","CAP_FACE",FACE,{"disambiguationData":[OSD([sQuery(id+"F4.wireOp",EDGE,"E13.9.0.0")])],"isStart":true});var subQ59=makeQuery(id+"F5.opExtrude","CAP_FACE",FACE,{"disambiguationData":[OSD([sQuery(id+"F4.wireOp",EDGE,"E14.0.14.0")])],"isStart":true});var subQ60=makeQuery(id+"F5.opExtrude","CAP_FACE",FACE,{"disambiguationData":[OSD([sQuery(id+"F4.wireOp",EDGE,"E14.0.15.0")])],"isStart":true});var subQ61=makeQuery(id+"F5.opExtrude","CAP_FACE",FACE,{"disambiguationData":[OSD([sQuery(id+"F4.wireOp",EDGE,"E14.0.17.0")])],"isStart":true});var subQ62=sQuery(id+"F4.wireOp",EDGE,"E14.0.19.0");var subQ63=makeQuery(id+"F5.opExtrude","SWEPT_FACE",FACE,{"disambiguationData":[OSD([subQ62])]});var subQ64=makeQuery(id+"F5.opExtrude","CAP_FACE",FACE,{"disambiguationData":[OSD([subQ62])],"isStart":true});var subQ65=sQuery(id+"F6.wireOp",EDGE,"E19.0.7.0");var subQ66=sQuery(id+"F2.wireOp",EDGE,"E8.left");Q1=makeQuery(id+"F7.boolean.opBoolean","SPLIT",FACE,{"disambiguationData":[TD([subQ37,subQ48,subQ40,subQ55,subQ29,subQ26,subQ24,subQ45,subQ25,subQ1,subQ46,subQ49,subQ51,subQ53,subQ43,subQ58,subQ10,subQ57,subQ7,subQ44,subQ39,subQ38,subQ27,subQ23,subQ30,subQ21,subQ22,subQ19,subQ20,subQ18,subQ14,subQ13,subQ16,subQ11,subQ12,subQ42,subQ56,subQ9,subQ41,subQ6,subQ8,subQ4,subQ5,subQ2,subQ3,subQ0,subQ47,subQ50,subQ52,subQ59,subQ60,subQ15,subQ61,subQ17,subQ63,subQ64,makeQuery(id+"F7.opExtrude","CAP_FACE",FACE,{"disambiguationData":[OSD([sQuery(id+"F6.wireOp",EDGE,"E18")])],"isStart":false}),makeQuery(id+"F7.opExtrude","CAP_FACE",FACE,{"disambiguationData":[OSD([sQuery(id+"F6.wireOp",EDGE,"E19.0.1.0")])],"isStart":false}),makeQuery(id+"F7.opExtrude","CAP_FACE",FACE,{"disambiguationData":[OSD([sQuery(id+"F6.wireOp",EDGE,"E19.0.2.0")])],"isStart":false}),makeQuery(id+"F7.opExtrude","CAP_FACE",FACE,{"disambiguationData":[OSD([sQuery(id+"F6.wireOp",EDGE,"E19.0.3.0")])],"isStart":false}),makeQuery(id+"F7.opExtrude","CAP_FACE",FACE,{"disambiguationData":[OSD([sQuery(id+"F6.wireOp",EDGE,"E19.0.4.0")])],"isStart":false}),makeQuery(id+"F7.opExtrude","CAP_FACE",FACE,{"disambiguationData":[OSD([sQuery(id+"F6.wireOp",EDGE,"E19.0.5.0")])],"isStart":false}),makeQuery(id+"F7.opExtrude","CAP_FACE",FACE,{"disambiguationData":[OSD([sQuery(id+"F6.wireOp",EDGE,"E19.0.6.0")])],"isStart":false}),makeQuery(id+"F7.opExtrude","SWEPT_FACE",FACE,{"disambiguationData":[OSD([subQ65])]}),makeQuery(id+"F7.opExtrude","CAP_FACE",FACE,{"disambiguationData":[OSD([subQ65])],"isStart":false})])],"derivedFrom":makeQuery(id+"F5.boolean.opBoolean","SPLIT",FACE,{"disambiguationData":[TD([subQ37,subQ48,subQ40,subQ55,makeQuery(id+"F3.opExtrude","CAP_FACE",FACE,{"disambiguationData":[OSD([subQ54,subQ28,subQ66,sQuery(id+"F2.wireOp",EDGE,"E8.right")])],"isStart":false}),subQ29,subQ26,subQ24,subQ45,subQ25,subQ1,subQ46,subQ49,subQ51,subQ53,subQ43,subQ58,subQ10,subQ57,subQ7,subQ44,subQ39,subQ38,subQ27,subQ23,subQ30,subQ21,subQ22,subQ19,subQ20,subQ18,subQ14,subQ13,subQ16,subQ11,subQ12,subQ42,subQ56,subQ9,subQ41,subQ6,subQ8,subQ4,subQ5,subQ2,subQ3,subQ0,subQ47,subQ50,subQ52,subQ59,subQ60,subQ15,subQ61,subQ17,subQ63,subQ64])],"derivedFrom":makeQuery(id+"F3.boolean.opBoolean","MERGE",FACE,{"derivedFrom":[makeQuery(id+"F1.opExtrude","SWEPT_FACE",FACE,{"disambiguationData":[OSD([subQ35])]}),makeQuery(id+"F3.opExtrude","SWEPT_FACE",FACE,{"disambiguationData":[OSD([subQ66])]})]})})});}
            extrude(context, id + "F9", {"entities" : qUnion([Q0]), "operationType" : NewBodyOperationType.ADD, "endBound" : BoundingType.UP_TO_SURFACE, "oppositeDirection" : true, "endBoundEntityFace" : qUnion([Q1]), "depth" : 25 * mm});
        }
        {
            var Q0;
            Q0=makeQuery(id+"F1.opExtrude","SWEPT_BODY",BODY,{"disambiguationData":[OSD([sQuery(id+"F0.wireOp",EDGE,"E0"),sQuery(id+"F0.wireOp",EDGE,"E1"),sQuery(id+"F0.wireOp",EDGE,"E2"),sQuery(id+"F0.wireOp",EDGE,"E3"),sQuery(id+"F0.wireOp",EDGE,"E4"),sQuery(id+"F0.wireOp",EDGE,"E5")])]});
            var Q1;
            Q1=qCreatedBy(makeId("Front.planeOp"),FACE);
            mirror(context, id + "F10", {"operationType" : NewBodyOperationType.ADD, "entities" : qUnion([Q0]), "mirrorPlane" : qUnion([Q1])});
        }
        {
            var Q0;
            Q0=makeQuery(id+"F1.opExtrude","SWEPT_BODY",BODY,{"disambiguationData":[OSD([sQuery(id+"F0.wireOp",EDGE,"E0"),sQuery(id+"F0.wireOp",EDGE,"E1"),sQuery(id+"F0.wireOp",EDGE,"E2"),sQuery(id+"F0.wireOp",EDGE,"E3"),sQuery(id+"F0.wireOp",EDGE,"E4"),sQuery(id+"F0.wireOp",EDGE,"E5")])]});
            var Q1;
            Q1=qCreatedBy(makeId("Right.planeOp"),FACE);
            mirror(context, id + "F11", {"operationType" : NewBodyOperationType.ADD, "entities" : qUnion([Q0]), "mirrorPlane" : qUnion([Q1])});
        }
        {
            var Q0;
            Q0=makeQuery(id+"F1.opExtrude","SWEPT_BODY",BODY,{"disambiguationData":[OSD([sQuery(id+"F0.wireOp",EDGE,"E0"),sQuery(id+"F0.wireOp",EDGE,"E1"),sQuery(id+"F0.wireOp",EDGE,"E2"),sQuery(id+"F0.wireOp",EDGE,"E3"),sQuery(id+"F0.wireOp",EDGE,"E4"),sQuery(id+"F0.wireOp",EDGE,"E5")])]});
            var Q1;
            Q1=makeQuery(id+"F10.opPattern","COPY",FACE,{"derivedFrom":makeQuery(id+"F3.opExtrude","CAP_FACE",FACE,{"disambiguationData":[OSD([sQuery(id+"F2.wireOp",EDGE,"E8.bottom"),sQuery(id+"F2.wireOp",EDGE,"E8.top"),sQuery(id+"F2.wireOp",EDGE,"E8.left"),sQuery(id+"F2.wireOp",EDGE,"E8.right")])],"isStart":false}),"instanceName":"1"});
            mirror(context, id + "F12", {"operationType" : NewBodyOperationType.ADD, "entities" : qUnion([Q0]), "mirrorPlane" : qUnion([Q1])});
        }
    });
